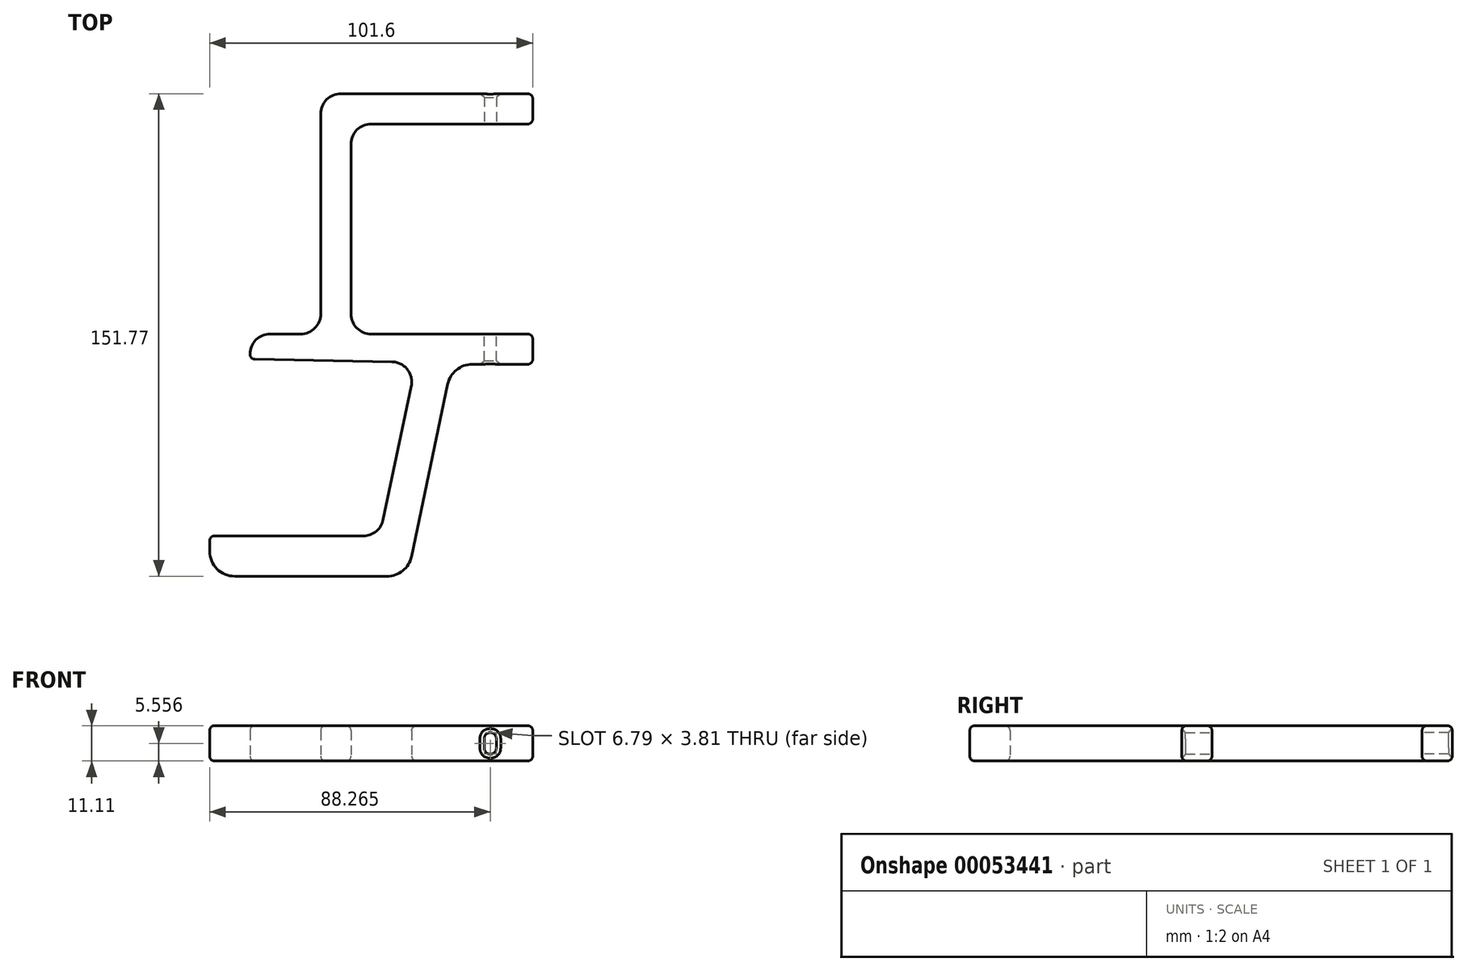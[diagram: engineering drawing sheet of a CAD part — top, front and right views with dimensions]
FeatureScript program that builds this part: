
annotation { "Feature Type Name" : "Feature", "Feature Type Description" : "" }
export const myFeature = defineFeature(function(context is Context, id is Id, definition is map)
    precondition{}
    {
        {
            var Q0;
            Q0=qCreatedBy(makeId("Top.planeOp"),FACE);
            var sketch = newSketch(context, id + "F0", { "sketchPlane" : qUnion([Q0])});
            skLineSegment(sketch, "E0", {"start": v(-88.9, -7.92) * mm, "end": v(-88.9, -8.26) * mm});
            skLineSegment(sketch, "E1", {"start": v(-101.6, -63.5) * mm, "end": v(-101.6, -68.28) * mm});
            skLineSegment(sketch, "E2", {"start": v(-18.97, -9.53) * mm, "end": v(0, -9.53) * mm});
            skLineSegment(sketch, "E3", {"start": v(0, -9.53) * mm, "end": v(0, 0) * mm});
            skLineSegment(sketch, "E4", {"start": v(-101.6, -63.5) * mm, "end": v(-53.25, -63.5) * mm});
            skLineSegment(sketch, "E5", {"start": v(-93.68, -76.2) * mm, "end": v(-45.86, -76.2) * mm});
            skPoint(sketch, "E6.visualSharp", {"position": v(-39.42, -76.2) * mm});
            skArc(sketch, "E7.filletArc", {"start": v(-101.6, -68.28) * mm, "mid": v(-99.28, -73.88) * mm, "end": v(-93.68, -76.2) * mm});
            skLineSegment(sketch, "E8", {"start": v(-38.1, -69.9) * mm, "end": v(-26.72, -15.82) * mm});
            skPoint(sketch, "E9.visualSharp", {"position": v(-25.4, -9.53) * mm});
            skArc(sketch, "E9.filletArc", {"start": v(-18.97, -9.53) * mm, "mid": v(-23.96, -11.3) * mm, "end": v(-26.72, -15.82) * mm});
            skArc(sketch, "E10.filletArc", {"start": v(-45.86, -76.2) * mm, "mid": v(-40.86, -74.43) * mm, "end": v(-38.1, -69.9) * mm});
            skLineSegment(sketch, "E11", {"start": v(-47.03, -58.46) * mm, "end": v(-38.19, -16.38) * mm});
            skLineSegment(sketch, "E12", {"start": v(-88.9, -7.92) * mm, "end": v(-44.29, -8.73) * mm});
            skPoint(sketch, "E13.visualSharp", {"position": v(-36.6, -8.87) * mm});
            skArc(sketch, "E13.filletArc", {"start": v(-38.19, -16.38) * mm, "mid": v(-39.43, -11.12) * mm, "end": v(-44.29, -8.73) * mm});
            skPoint(sketch, "E14.visualSharp", {"position": v(-48.1, -63.5) * mm});
            skArc(sketch, "E14.filletArc", {"start": v(-53.25, -63.5) * mm, "mid": v(-49.25, -62.08) * mm, "end": v(-47.03, -58.46) * mm});
            skLineSegment(sketch, "E15", {"start": v(0, 0) * mm, "end": v(-50.8, 0) * mm});
            skLineSegment(sketch, "E16", {"start": v(-57.15, 6.35) * mm, "end": v(-57.15, 59.7) * mm});
            skLineSegment(sketch, "E17", {"start": v(-60.33, 75.57) * mm, "end": v(0, 75.57) * mm});
            skLineSegment(sketch, "E18", {"start": v(0, 66.04) * mm, "end": v(0, 75.57) * mm});
            skLineSegment(sketch, "E19", {"start": v(0, 66.04) * mm, "end": v(-50.8, 66.04) * mm});
            skLineSegment(sketch, "E20", {"start": v(-73.03, 0) * mm, "end": v(-82.55, 0) * mm});
            skLineSegment(sketch, "E21", {"start": v(-88.9, -6.35) * mm, "end": v(-88.9, -7.92) * mm});
            skLineSegment(sketch, "E22", {"start": v(-66.68, 6.35) * mm, "end": v(-66.68, 69.22) * mm});
            skPoint(sketch, "E23.visualSharp", {"position": v(-57.15, 66.04) * mm});
            skArc(sketch, "E23.filletArc", {"start": v(-50.8, 66.04) * mm, "mid": v(-55.3, 64.18) * mm, "end": v(-57.15, 59.7) * mm});
            skPoint(sketch, "E24.visualSharp", {"position": v(-57.15, 0) * mm});
            skArc(sketch, "E24.filletArc", {"start": v(-57.15, 6.35) * mm, "mid": v(-55.3, 1.86) * mm, "end": v(-50.8, 0) * mm});
            skPoint(sketch, "E25.visualSharp", {"position": v(-66.68, 0) * mm});
            skArc(sketch, "E25.filletArc", {"start": v(-73.03, 0) * mm, "mid": v(-68.53, 1.86) * mm, "end": v(-66.68, 6.35) * mm});
            skPoint(sketch, "E26.visualSharp", {"position": v(-66.68, 75.57) * mm});
            skArc(sketch, "E26.filletArc", {"start": v(-60.33, 75.57) * mm, "mid": v(-64.82, 73.7) * mm, "end": v(-66.68, 69.22) * mm});
            skPoint(sketch, "E27.visualSharp", {"position": v(0, 75.57) * mm});
            skPoint(sketch, "E28.visualSharp", {"position": v(-88.9, 0) * mm});
            skArc(sketch, "E28.filletArc", {"start": v(-82.55, 0) * mm, "mid": v(-87.04, -1.86) * mm, "end": v(-88.9, -6.35) * mm});
            skSolve(sketch);
        }
        {
            var Q0;
            Q0=makeQuery(id+"F0.imprint","IMPRINT",FACE,{"disambiguationData":[TD([[makeQuery(id+"F0.imprint","IMPRINT",EDGE,{"derivedFrom":sQuery(id+"F0.wireOp",EDGE,"E1")}),1.0]])]});
            extrude(context, id + "F1", {"entities" : qUnion([Q0]), "depth" : 11.1 * mm});
        }
        {
            var Q0;
            Q0=qCreatedBy(makeId("Front.planeOp"),FACE);
            var sketch = newSketch(context, id + "F2", { "sketchPlane" : qUnion([Q0])});
            skArc(sketch, "E29", {"start": v(-15.24, 4.06) * mm, "mid": v(-13.34, 2.16) * mm, "end": v(-11.43, 4.06) * mm});
            skArc(sketch, "E30", {"start": v(-11.43, 7.05) * mm, "mid": v(-13.34, 8.95) * mm, "end": v(-15.24, 7.05) * mm});
            skLineSegment(sketch, "E31", {"start": v(-15.24, 7.05) * mm, "end": v(-15.24, 4.06) * mm});
            skLineSegment(sketch, "E32", {"start": v(-11.43, 7.05) * mm, "end": v(-11.43, 4.06) * mm});
            skSolve(sketch);
        }
        {
            var Q0;
            Q0 = qSketchRegion(id + "F2", true);
            extrude(context, id + "F3", {"entities" : qUnion([Q0]), "operationType" : NewBodyOperationType.REMOVE, "endBound" : BoundingType.THROUGH_ALL, "depth" : 25.4 * mm});
        }
        {
            var Q0;
            Q0 = qSketchRegion(id + "F2", true);
            extrude(context, id + "F4", {"entities" : qUnion([Q0]), "operationType" : NewBodyOperationType.REMOVE, "endBound" : BoundingType.THROUGH_ALL, "oppositeDirection" : true, "depth" : 25.4 * mm});
        }
        {
            var Q0;
            Q0=makeQuery(id+"F3.boolean.opBoolean","INTERSECT",EDGE,{"derivedFrom":[makeQuery(id+"F1.opExtrude","SWEPT_FACE",FACE,{"disambiguationData":[OSD([sQuery(id+"F0.wireOp",EDGE,"E2")])]}),makeQuery(id+"F3.opExtrude","SWEPT_FACE",FACE,{"disambiguationData":[OSD([sQuery(id+"F2.wireOp",EDGE,"E31")])]})]});
            var Q1;
            Q1=makeQuery(id+"F3.boolean.opBoolean","INTERSECT",EDGE,{"derivedFrom":[makeQuery(id+"F1.opExtrude","SWEPT_FACE",FACE,{"disambiguationData":[OSD([sQuery(id+"F0.wireOp",EDGE,"E2")])]}),makeQuery(id+"F3.opExtrude","SWEPT_FACE",FACE,{"disambiguationData":[OSD([sQuery(id+"F2.wireOp",EDGE,"E29")])]})]});
            var Q2;
            Q2=makeQuery(id+"F3.boolean.opBoolean","INTERSECT",EDGE,{"derivedFrom":[makeQuery(id+"F1.opExtrude","SWEPT_FACE",FACE,{"disambiguationData":[OSD([sQuery(id+"F0.wireOp",EDGE,"E2")])]}),makeQuery(id+"F3.opExtrude","SWEPT_FACE",FACE,{"disambiguationData":[OSD([sQuery(id+"F2.wireOp",EDGE,"E32")])]})]});
            var Q3;
            Q3=makeQuery(id+"F3.boolean.opBoolean","INTERSECT",EDGE,{"derivedFrom":[makeQuery(id+"F1.opExtrude","SWEPT_FACE",FACE,{"disambiguationData":[OSD([sQuery(id+"F0.wireOp",EDGE,"E2")])]}),makeQuery(id+"F3.opExtrude","SWEPT_FACE",FACE,{"disambiguationData":[OSD([sQuery(id+"F2.wireOp",EDGE,"E30")])]})]});
            var Q4;
            Q4=makeQuery(id+"F4.boolean.opBoolean","INTERSECT",EDGE,{"derivedFrom":[makeQuery(id+"F1.opExtrude","SWEPT_FACE",FACE,{"disambiguationData":[OSD([sQuery(id+"F0.wireOp",EDGE,"E17")])]}),makeQuery(id+"F4.opExtrude","SWEPT_FACE",FACE,{"disambiguationData":[OSD([sQuery(id+"F2.wireOp",EDGE,"E29")])]})]});
            chamfer(context, id + "F5", {"entities" : qUnion([Q0, Q1, Q2, Q3, Q4]), "chamferType" : ChamferType.OFFSET_ANGLE, "width" : 1.14 * mm, "oppositeDirection" : false, "angle" : 50 * degree, "tangentPropagation" : true});
        }
        {
            var Q0;
            Q0=makeQuery(id+"F1.opExtrude","SWEPT_FACE",FACE,{"disambiguationData":[OSD([sQuery(id+"F0.wireOp",EDGE,"E11")])]});
            var Q1;
            Q1=makeQuery(id+"F1.opExtrude","SWEPT_FACE",FACE,{"disambiguationData":[OSD([sQuery(id+"F0.wireOp",EDGE,"E1")])]});
            var Q2;
            Q2=makeQuery(id+"F1.opExtrude","SWEPT_FACE",FACE,{"disambiguationData":[OSD([sQuery(id+"F0.wireOp",EDGE,"1aaa925a-bd7c-41a2-88cc-1a931677daa7")])]});
            var Q3;
            Q3=makeQuery(id+"F1.opExtrude","SWEPT_FACE",FACE,{"disambiguationData":[OSD([sQuery(id+"F0.wireOp",EDGE,"a0ca3ada-2ed9-4292-aa87-304cbc1274c1.filletArc")])]});
            var Q4;
            Q4=makeQuery(id+"F1.opExtrude","SWEPT_FACE",FACE,{"disambiguationData":[OSD([sQuery(id+"F0.wireOp",EDGE,"E3")])]});
            var Q5;
            Q5=makeQuery(id+"F1.opExtrude","SWEPT_EDGE",EDGE,{"disambiguationData":[OSD([sQuery(id+"F0.wireOp",EDGE,"ed241437-909b-430b-bc63-bb90648ee461.filletArc"),sQuery(id+"F0.wireOp",EDGE,"E12")])]});
            var Q6;
            Q6=makeQuery(id+"F1.opExtrude","SWEPT_FACE",FACE,{"disambiguationData":[OSD([sQuery(id+"F0.wireOp",EDGE,"E18")])]});
            var Q7;
            Q7=makeQuery(id+"F1.opExtrude","CAP_FACE",FACE,{"disambiguationData":[OSD([sQuery(id+"F0.wireOp",EDGE,"E1"),sQuery(id+"F0.wireOp",EDGE,"E2"),sQuery(id+"F0.wireOp",EDGE,"E3"),sQuery(id+"F0.wireOp",EDGE,"E4"),sQuery(id+"F0.wireOp",EDGE,"E5"),sQuery(id+"F0.wireOp",EDGE,"E7.filletArc"),sQuery(id+"F0.wireOp",EDGE,"E8"),sQuery(id+"F0.wireOp",EDGE,"E9.filletArc"),sQuery(id+"F0.wireOp",EDGE,"E10.filletArc"),sQuery(id+"F0.wireOp",EDGE,"E11"),sQuery(id+"F0.wireOp",EDGE,"E12"),sQuery(id+"F0.wireOp",EDGE,"E13.filletArc"),sQuery(id+"F0.wireOp",EDGE,"E14.filletArc"),sQuery(id+"F0.wireOp",EDGE,"E15"),sQuery(id+"F0.wireOp",EDGE,"E16"),sQuery(id+"F0.wireOp",EDGE,"E17"),sQuery(id+"F0.wireOp",EDGE,"E18"),sQuery(id+"F0.wireOp",EDGE,"E19"),sQuery(id+"F0.wireOp",EDGE,"E20"),sQuery(id+"F0.wireOp",EDGE,"E21"),sQuery(id+"F0.wireOp",EDGE,"E22"),sQuery(id+"F0.wireOp",EDGE,"E23.filletArc"),sQuery(id+"F0.wireOp",EDGE,"E24.filletArc"),sQuery(id+"F0.wireOp",EDGE,"E25.filletArc"),sQuery(id+"F0.wireOp",EDGE,"E26.filletArc"),sQuery(id+"F0.wireOp",EDGE,"E28.filletArc")])],"isStart":false});
            var Q8;
            Q8=makeQuery(id+"F1.opExtrude","CAP_FACE",FACE,{"disambiguationData":[OSD([sQuery(id+"F0.wireOp",EDGE,"E1"),sQuery(id+"F0.wireOp",EDGE,"E2"),sQuery(id+"F0.wireOp",EDGE,"E3"),sQuery(id+"F0.wireOp",EDGE,"E4"),sQuery(id+"F0.wireOp",EDGE,"E5"),sQuery(id+"F0.wireOp",EDGE,"E7.filletArc"),sQuery(id+"F0.wireOp",EDGE,"E8"),sQuery(id+"F0.wireOp",EDGE,"E9.filletArc"),sQuery(id+"F0.wireOp",EDGE,"E10.filletArc"),sQuery(id+"F0.wireOp",EDGE,"E11"),sQuery(id+"F0.wireOp",EDGE,"E12"),sQuery(id+"F0.wireOp",EDGE,"E13.filletArc"),sQuery(id+"F0.wireOp",EDGE,"E14.filletArc"),sQuery(id+"F0.wireOp",EDGE,"E15"),sQuery(id+"F0.wireOp",EDGE,"E16"),sQuery(id+"F0.wireOp",EDGE,"E17"),sQuery(id+"F0.wireOp",EDGE,"E18"),sQuery(id+"F0.wireOp",EDGE,"E19"),sQuery(id+"F0.wireOp",EDGE,"E20"),sQuery(id+"F0.wireOp",EDGE,"E21"),sQuery(id+"F0.wireOp",EDGE,"E22"),sQuery(id+"F0.wireOp",EDGE,"E23.filletArc"),sQuery(id+"F0.wireOp",EDGE,"E24.filletArc"),sQuery(id+"F0.wireOp",EDGE,"E25.filletArc"),sQuery(id+"F0.wireOp",EDGE,"E26.filletArc"),sQuery(id+"F0.wireOp",EDGE,"E28.filletArc")])],"isStart":true});
            fillet(context, id + "F6", {"entities" : qUnion([Q0, Q1, Q2, Q3, Q4, Q5, Q6, Q7, Q8]), "radius" : 1.57 * mm, "tangentPropagation" : true, "allowEdgeOverflow" : false});
        }
    });
